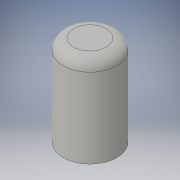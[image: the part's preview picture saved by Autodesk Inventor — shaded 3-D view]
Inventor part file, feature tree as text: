
AUTODESK INVENTOR PART (.ipt)
format: ipt  version: 2016 (Build 200138000, 138)  size: 104,960 bytes
history: native  units: in
note: dims shown in document units (in); Inventor stores cm internally (conversion verified against a paired STEP export)
features: extrude x1, fillet x1, sketch x1
ambient origin geometry x8: Origin, YZ Plane, XZ Plane, XY Plane, X Axis, Y Axis, Z Axis, Center Point
bodies: Solid1 (feature_tree)
feature tree (3):
  extrude  "Extrusion1"  Depth=0.6614in TaperAngle=0.0deg
  fillet  "Fillet1"  Radius=0.0787in
  sketch  "Sketch1"  dims[d0=0.3937in d1=0.6614in d2=0.0in d3=0.0787in]
